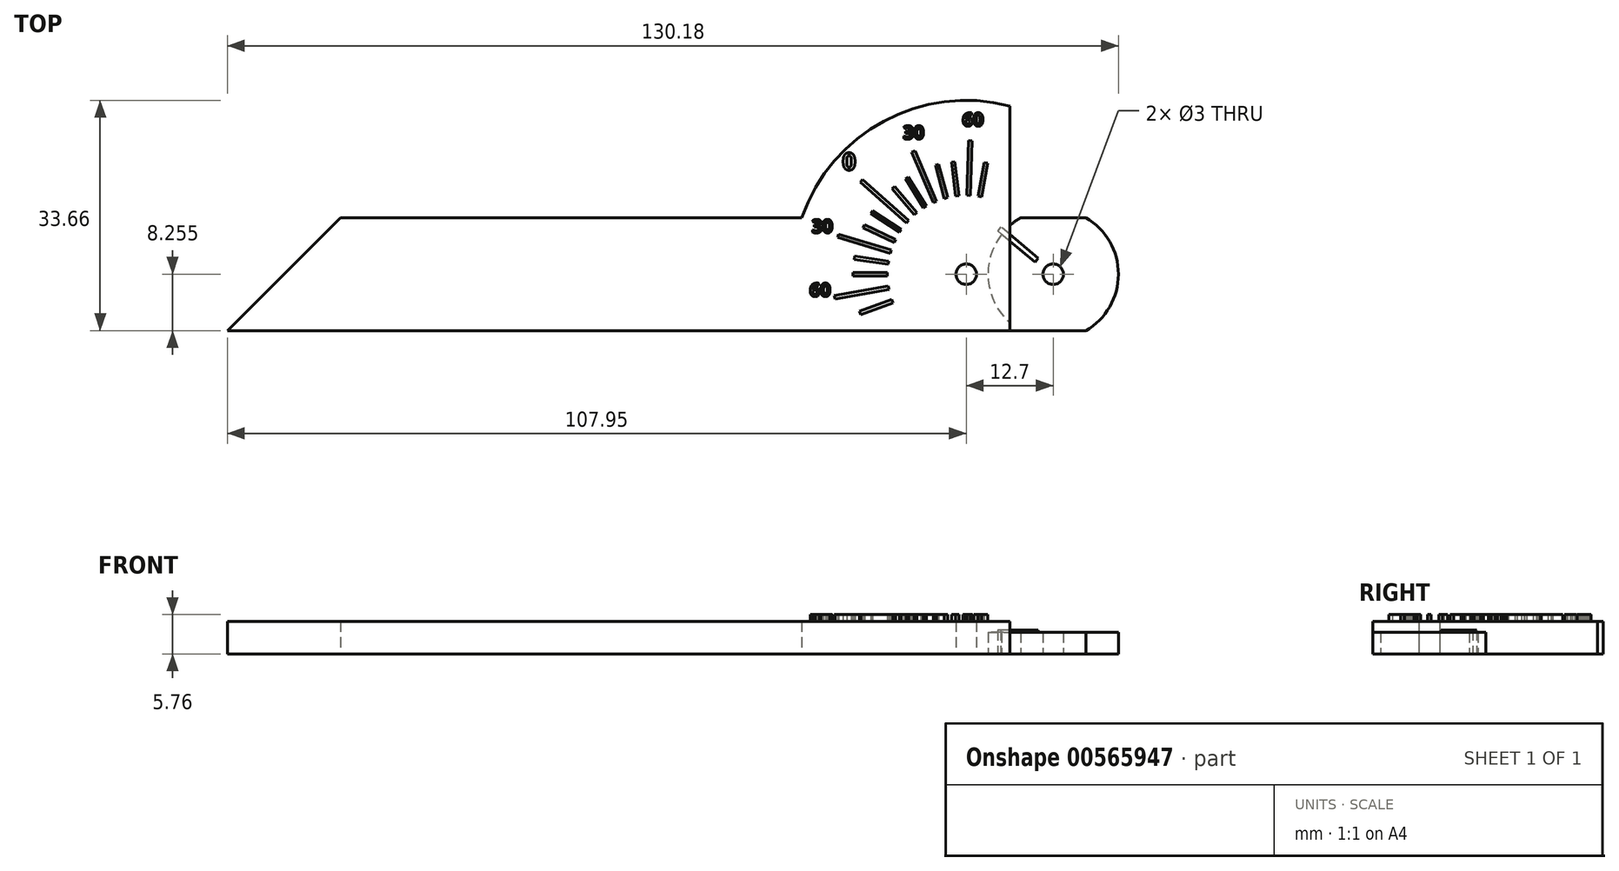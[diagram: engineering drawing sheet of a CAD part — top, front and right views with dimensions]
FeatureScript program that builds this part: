
annotation { "Feature Type Name" : "Feature", "Feature Type Description" : "" }
export const myFeature = defineFeature(function(context is Context, id is Id, definition is map)
    precondition{}
    {
        {
            var Q0;
            Q0=qCreatedBy(makeId("Top.planeOp"),FACE);
            var sketch = newSketch(context, id + "F0", { "sketchPlane" : qUnion([Q0])});
            skLineSegment(sketch, "E0.bottom", {"start": v(0, 0) * mm, "end": v(114.3, 0) * mm});
            skLineSegment(sketch, "E0.top", {"start": v(0, 16.51) * mm, "end": v(97.79, 16.51) * mm});
            skLineSegment(sketch, "E0.left", {"start": v(0, 0) * mm, "end": v(0, 16.51) * mm});
            skLineSegment(sketch, "E1", {"start": v(114.3, 0) * mm, "end": v(97.79, 16.51) * mm});
            skCircle(sketch, "E2", {"center": v(6.35, 8.26) * mm, "radius": 9.53 * mm});
            skPoint(sketch, "E2.centerSnap0", {"position": v(0, 8.26) * mm});
            skLineSegment(sketch, "E3", {"start": v(-7.35, 8.26) * mm, "end": v(-3.17, 8.26) * mm, "construction": true});
            skCircle(sketch, "E4", {"center": v(6.35, 8.26) * mm, "radius": 1.5 * mm});
            skLineSegment(sketch, "E5", {"start": v(11.1, 0) * mm, "end": v(0, 0) * mm});
            skLineSegment(sketch, "E6", {"start": v(11.1, 16.51) * mm, "end": v(0, 16.51) * mm});
            skLineSegment(sketch, "E7", {"start": v(6.35, 8.26) * mm, "end": v(-14.53, 8.26) * mm, "construction": true});
            skLineSegment(sketch, "E8", {"start": v(-14.53, 8.26) * mm, "end": v(6.35, 8.26) * mm, "construction": true});
            skLineSegment(sketch, "E9", {"start": v(6.35, 8.25) * mm, "end": v(-8.62, 20.82) * mm, "construction": true});
            skLineSegment(sketch, "E10", {"start": v(3.92, 10.3) * mm, "end": v(4.16, 10.58) * mm});
            skLineSegment(sketch, "E11", {"start": v(4.16, 10.58) * mm, "end": v(-1.3, 15.16) * mm});
            skLineSegment(sketch, "E12", {"start": v(-1.3, 15.16) * mm, "end": v(-1.54, 14.87) * mm});
            skLineSegment(sketch, "E13.MirrorCS", {"start": v(-1.78, 14.59) * mm, "end": v(-1.54, 14.87) * mm});
            skLineSegment(sketch, "E14.MirrorCS", {"start": v(3.68, 10) * mm, "end": v(-1.78, 14.59) * mm});
            skLineSegment(sketch, "E15.MirrorCS", {"start": v(3.92, 10.3) * mm, "end": v(3.68, 10) * mm});
            skPoint(sketch, "E16", {"position": v(-0.7, 14.66) * mm});
            skPoint(sketch, "E17.orphan", {"position": v(0, 9.02) * mm});
            skPoint(sketch, "E18.MirrorCS.start.orphan", {"position": v(-7.35, 9.02) * mm});
            skPoint(sketch, "E19.orphan", {"position": v(0, 7.49) * mm});
            skPoint(sketch, "E20.end.orphan", {"position": v(-7.35, 7.49) * mm});
            skPoint(sketch, "E21.MirrorCS.start.orphan", {"position": v(-7.35, 8.26) * mm});
            skSolve(sketch);
        }
        {
            var Q0;
            {var subQ0=sQuery(id+"F0.wireOp",EDGE,"E0.bottom");Q0=makeQuery(id+"F0.imprint","IMPRINT",FACE,{"disambiguationData":[TD([[makeQuery(id+"F0.imprint","IMPRINT",EDGE,{"derivedFrom":subQ0}),1.0]])]});}
            var Q1;
            Q1=makeQuery(id+"F0.imprint","IMPRINT",FACE,{"disambiguationData":[TD([[makeQuery(id+"F0.imprint","IMPRINT",EDGE,{"derivedFrom":sQuery(id+"F0.wireOp",EDGE,"E4")}),-1.0]])]});
            var Q2;
            {var subQ0=sQuery(id+"F0.wireOp",EDGE,"E2");var subQ1=sQuery(id+"F0.wireOp",EDGE,"E0.left");var subQ2=makeQuery(id+"F0.imprint","INTERSECT",VERTEX,{"disambiguationData":[OD(0.0)],"derivedFrom":[subQ1,subQ0]});Q2=makeQuery(id+"F0.imprint","IMPRINT",FACE,{"disambiguationData":[TD([[makeQuery(id+"F0.imprint","IMPRINT",EDGE,{"disambiguationData":[TD([[subQ2,-1.0]])],"derivedFrom":subQ1}),1.0]])]});}
            extrude(context, id + "F1", {"entities" : qUnion([Q0, Q1, Q2]), "depth" : 3.17 * mm, "offsetDistance" : 25.4 * mm});
        }
        {
            var Q0;
            {var subQ5=sQuery(id+"F0.wireOp",EDGE,"E0.left");var subQ7=sQuery(id+"F0.wireOp",EDGE,"E14.MirrorCS");var subQ9=makeQuery(id+"F0.imprint","INTERSECT",VERTEX,{"derivedFrom":[subQ5,subQ7]});Q0=makeQuery(id+"F0.imprint","IMPRINT",FACE,{"disambiguationData":[TD([[makeQuery(id+"F0.imprint","IMPRINT",EDGE,{"disambiguationData":[TD([[subQ9,-1.0]])],"derivedFrom":subQ5}),1.0]])]});}
            var Q1;
            {var subQ1=sQuery(id+"F0.wireOp",EDGE,"E10");Q1=makeQuery(id+"F0.imprint","IMPRINT",FACE,{"disambiguationData":[TD([[makeQuery(id+"F0.imprint","IMPRINT",EDGE,{"derivedFrom":subQ1}),1.0]])]});}
            var Q2;
            {var subQ0=sQuery(id+"F0.wireOp",EDGE,"E12");Q2=makeQuery(id+"F0.imprint","IMPRINT",FACE,{"disambiguationData":[TD([[makeQuery(id+"F0.imprint","IMPRINT",EDGE,{"derivedFrom":subQ0}),1.0]])]});}
            var Q3;
            {var subQ0=sQuery(id+"F0.wireOp",EDGE,"E13.MirrorCS");Q3=makeQuery(id+"F0.imprint","IMPRINT",FACE,{"disambiguationData":[TD([[makeQuery(id+"F0.imprint","IMPRINT",EDGE,{"derivedFrom":subQ0}),-1.0]])]});}
            extrude(context, id + "F2", {"entities" : qUnion([Q0, Q1, Q2, Q3]), "operationType" : NewBodyOperationType.ADD, "depth" : 3.5 * mm, "offsetDistance" : 25.4 * mm});
        }
        {
            var Q0;
            Q0=qCreatedBy(makeId("Top.planeOp"),FACE);
            var sketch = newSketch(context, id + "F3", { "sketchPlane" : qUnion([Q0])});
            skLineSegment(sketch, "E22.bottom", {"start": v(0, 0) * mm, "end": v(-114.3, 0) * mm});
            skLineSegment(sketch, "E22.top", {"start": v(0, 16.51) * mm, "end": v(-97.8, 16.51) * mm});
            skLineSegment(sketch, "E22.left", {"start": v(0, 0) * mm, "end": v(0, 16.51) * mm});
            skLineSegment(sketch, "E23", {"start": v(-114.3, 0) * mm, "end": v(-97.8, 16.5) * mm});
            skCircle(sketch, "E24", {"center": v(-6.35, 8.26) * mm, "radius": 25.4 * mm});
            skPoint(sketch, "E24.centerSnap0", {"position": v(0, 8.26) * mm});
            skLineSegment(sketch, "E25", {"start": v(-6.35, 8.26) * mm, "end": v(0, 8.26) * mm});
            skLineSegment(sketch, "E26", {"start": v(0, 16.51) * mm, "end": v(17.67, 16.51) * mm});
            skLineSegment(sketch, "E27", {"start": v(0, 0) * mm, "end": v(17.67, 0) * mm});
            skCircle(sketch, "E28", {"center": v(-6.35, 8.26) * mm, "radius": 1.5 * mm});
            skLineSegment(sketch, "E29", {"start": v(0, 16.51) * mm, "end": v(0, 32.85) * mm});
            skSolve(sketch);
        }
        {
            var Q0;
            {var subQ0=sQuery(id+"F3.wireOp",EDGE,"E23");Q0=makeQuery(id+"F3.imprint","IMPRINT",FACE,{"disambiguationData":[TD([[makeQuery(id+"F3.imprint","IMPRINT",EDGE,{"derivedFrom":subQ0}),-1.0]])]});}
            var Q1;
            Q1=makeQuery(id+"F3.imprint","IMPRINT",FACE,{"disambiguationData":[TD([[makeQuery(id+"F3.imprint","IMPRINT",EDGE,{"derivedFrom":sQuery(id+"F3.wireOp",EDGE,"E28")}),-1.0]])]});
            var Q2;
            {var subQ0=sQuery(id+"F3.wireOp",EDGE,"E29");Q2=makeQuery(id+"F3.imprint","IMPRINT",FACE,{"disambiguationData":[TD([[makeQuery(id+"F3.imprint","IMPRINT",EDGE,{"derivedFrom":subQ0}),1.0]])]});}
            extrude(context, id + "F4", {"entities" : qUnion([Q0, Q1, Q2]), "depth" : 4.76 * mm, "offsetDistance" : 25.4 * mm});
        }
        {
            var Q0;
            Q0=makeQuery(id+"F4.opExtrude","CAP_FACE",FACE,{"disambiguationData":[OSD([sQuery(id+"F3.wireOp",EDGE,"E22.bottom"),sQuery(id+"F3.wireOp",EDGE,"E22.top"),sQuery(id+"F3.wireOp",EDGE,"E22.left"),sQuery(id+"F3.wireOp",EDGE,"E23"),sQuery(id+"F3.wireOp",EDGE,"E24"),sQuery(id+"F3.wireOp",EDGE,"E28"),sQuery(id+"F3.wireOp",EDGE,"E29")])],"isStart":false});
            var sketch = newSketch(context, id + "F5", { "sketchPlane" : qUnion([Q0])});
            skCircle(sketch, "E30", {"center": v(-6.35, 8.26) * mm, "radius": 9.53 * mm});
            skCircle(sketch, "E31.0", {"center": v(-6.35, 8.26) * mm, "radius": 11.53 * mm});
            skLineSegment(sketch, "E32", {"start": v(-6.35, 8.26) * mm, "end": v(-38.76, 8.25) * mm, "construction": true});
            skLineSegment(sketch, "E33", {"start": v(-17.88, 8.25) * mm, "end": v(-17.88, 8.5) * mm});
            skLineSegment(sketch, "E34", {"start": v(-17.88, 8.5) * mm, "end": v(-22.88, 8.5) * mm});
            skLineSegment(sketch, "E35", {"start": v(-22.88, 8.5) * mm, "end": v(-22.88, 8.25) * mm});
            skLineSegment(sketch, "E36.MirrorCS", {"start": v(-17.88, 8) * mm, "end": v(-22.88, 8) * mm});
            skLineSegment(sketch, "E37.MirrorCS", {"start": v(-22.88, 8) * mm, "end": v(-22.88, 8.25) * mm});
            skLineSegment(sketch, "E38.MirrorCS", {"start": v(-17.88, 8.26) * mm, "end": v(-17.88, 8) * mm});
            skSolve(sketch);
        }
        {
            var Q0;
            {var subQ2=sQuery(id+"F5.wireOp",EDGE,"E33");Q0=makeQuery(id+"F5.imprint","IMPRINT",FACE,{"disambiguationData":[TD([[makeQuery(id+"F5.imprint","IMPRINT",EDGE,{"derivedFrom":subQ2}),-1.0]])]});}
            var sketch = newSketch(context, id + "F6", { "sketchPlane" : qUnion([Q0])});
            skLineSegment(sketch, "E39.0", {"start": v(-17.88, 8.25) * mm, "end": v(-17.88, 8.5) * mm});
            skLineSegment(sketch, "E40.0", {"start": v(-17.88, 8.26) * mm, "end": v(-17.88, 8) * mm});
            skLineSegment(sketch, "E41.0", {"start": v(-17.88, 8) * mm, "end": v(-22.88, 8) * mm});
            skLineSegment(sketch, "E42.0", {"start": v(-17.88, 8.5) * mm, "end": v(-22.88, 8.5) * mm});
            skLineSegment(sketch, "E43.0", {"start": v(-22.88, 8.5) * mm, "end": v(-22.88, 8.25) * mm});
            skLineSegment(sketch, "E44.0", {"start": v(-22.88, 8) * mm, "end": v(-22.88, 8.25) * mm});
            skPoint(sketch, "E45.0", {"position": v(-6.35, 8.26) * mm});
            skLineSegment(sketch, "E46", {"start": v(-22.88, 8) * mm, "end": v(-17.88, 8.5) * mm, "construction": true});
            skLineSegment(sketch, "E47", {"start": v(-22.88, 8.5) * mm, "end": v(-17.88, 8) * mm, "construction": true});
            skPoint(sketch, "E48", {"position": v(-20.38, 8.25) * mm});
            skLineSegment(sketch, "E49.1.0", {"start": v(-17.79, 9.68) * mm, "end": v(-22.74, 10.4) * mm});
            skLineSegment(sketch, "E49.1.1", {"start": v(-22.74, 10.4) * mm, "end": v(-17.72, 10.17) * mm, "construction": true});
            skLineSegment(sketch, "E49.1.2", {"start": v(-22.66, 10.9) * mm, "end": v(-17.79, 9.68) * mm, "construction": true});
            skLineSegment(sketch, "E49.1.3", {"start": v(-17.75, 9.93) * mm, "end": v(-17.72, 10.17) * mm});
            skLineSegment(sketch, "E49.1.4", {"start": v(-17.75, 9.93) * mm, "end": v(-17.79, 9.68) * mm});
            skLineSegment(sketch, "E49.1.5", {"start": v(-22.66, 10.9) * mm, "end": v(-17.72, 10.17) * mm});
            skLineSegment(sketch, "E49.1.6", {"start": v(-22.74, 10.4) * mm, "end": v(-22.7, 10.65) * mm});
            skLineSegment(sketch, "E49.1.7", {"start": v(-22.66, 10.9) * mm, "end": v(-22.7, 10.65) * mm});
            skPoint(sketch, "E49.1.8", {"position": v(-20.23, 10.29) * mm});
            skLineSegment(sketch, "E49.2.0", {"start": v(-17.46, 11.32) * mm, "end": v(-22.25, 12.75) * mm});
            skLineSegment(sketch, "E49.2.1", {"start": v(-22.25, 12.75) * mm, "end": v(-17.32, 11.8) * mm, "construction": true});
            skLineSegment(sketch, "E49.2.2", {"start": v(-22.1, 13.23) * mm, "end": v(-17.46, 11.32) * mm, "construction": true});
            skLineSegment(sketch, "E49.2.3", {"start": v(-17.4, 11.56) * mm, "end": v(-17.32, 11.8) * mm});
            skLineSegment(sketch, "E49.2.4", {"start": v(-17.4, 11.56) * mm, "end": v(-17.46, 11.32) * mm});
            skLineSegment(sketch, "E49.2.5", {"start": v(-22.1, 13.23) * mm, "end": v(-17.32, 11.8) * mm});
            skLineSegment(sketch, "E49.2.6", {"start": v(-22.25, 12.75) * mm, "end": v(-22.18, 13) * mm});
            skLineSegment(sketch, "E49.2.7", {"start": v(-22.1, 13.23) * mm, "end": v(-22.18, 13) * mm});
            skPoint(sketch, "E49.2.8", {"position": v(-19.79, 12.28) * mm});
            skLineSegment(sketch, "E49.3.0", {"start": v(-16.9, 12.9) * mm, "end": v(-21.43, 15.01) * mm});
            skLineSegment(sketch, "E49.3.1", {"start": v(-21.43, 15.01) * mm, "end": v(-16.69, 13.35) * mm, "construction": true});
            skLineSegment(sketch, "E49.3.2", {"start": v(-21.22, 15.47) * mm, "end": v(-16.9, 12.9) * mm, "construction": true});
            skLineSegment(sketch, "E49.3.3", {"start": v(-16.8, 13.13) * mm, "end": v(-16.69, 13.35) * mm});
            skLineSegment(sketch, "E49.3.4", {"start": v(-16.8, 13.13) * mm, "end": v(-16.9, 12.9) * mm});
            skLineSegment(sketch, "E49.3.5", {"start": v(-21.22, 15.47) * mm, "end": v(-16.69, 13.35) * mm});
            skLineSegment(sketch, "E49.3.6", {"start": v(-21.43, 15.01) * mm, "end": v(-21.33, 15.24) * mm});
            skLineSegment(sketch, "E49.3.7", {"start": v(-21.22, 15.47) * mm, "end": v(-21.33, 15.24) * mm});
            skPoint(sketch, "E49.3.8", {"position": v(-19.06, 14.18) * mm});
            skLineSegment(sketch, "E49.4.0", {"start": v(-16.12, 14.38) * mm, "end": v(-20.3, 17.13) * mm});
            skLineSegment(sketch, "E49.4.1", {"start": v(-20.3, 17.13) * mm, "end": v(-15.84, 14.8) * mm, "construction": true});
            skLineSegment(sketch, "E49.4.2", {"start": v(-20.02, 17.54) * mm, "end": v(-16.12, 14.38) * mm, "construction": true});
            skLineSegment(sketch, "E49.4.3", {"start": v(-15.98, 14.59) * mm, "end": v(-15.84, 14.8) * mm});
            skLineSegment(sketch, "E49.4.4", {"start": v(-15.98, 14.59) * mm, "end": v(-16.12, 14.38) * mm});
            skLineSegment(sketch, "E49.4.5", {"start": v(-20.02, 17.54) * mm, "end": v(-15.84, 14.8) * mm});
            skLineSegment(sketch, "E49.4.6", {"start": v(-20.3, 17.13) * mm, "end": v(-20.16, 17.34) * mm});
            skLineSegment(sketch, "E49.4.7", {"start": v(-20.02, 17.54) * mm, "end": v(-20.16, 17.34) * mm});
            skPoint(sketch, "E49.4.8", {"position": v(-18.07, 15.96) * mm});
            skLineSegment(sketch, "E49.5.0", {"start": v(-15.13, 15.73) * mm, "end": v(-18.86, 19.05) * mm});
            skLineSegment(sketch, "E49.5.1", {"start": v(-18.86, 19.05) * mm, "end": v(-14.8, 16.1) * mm, "construction": true});
            skLineSegment(sketch, "E49.5.2", {"start": v(-18.53, 19.43) * mm, "end": v(-15.13, 15.73) * mm, "construction": true});
            skLineSegment(sketch, "E49.5.3", {"start": v(-14.96, 15.92) * mm, "end": v(-14.8, 16.1) * mm});
            skLineSegment(sketch, "E49.5.4", {"start": v(-14.96, 15.92) * mm, "end": v(-15.13, 15.73) * mm});
            skLineSegment(sketch, "E49.5.5", {"start": v(-18.53, 19.43) * mm, "end": v(-14.8, 16.1) * mm});
            skLineSegment(sketch, "E49.5.6", {"start": v(-18.86, 19.05) * mm, "end": v(-18.7, 19.24) * mm});
            skLineSegment(sketch, "E49.5.7", {"start": v(-18.53, 19.43) * mm, "end": v(-18.7, 19.24) * mm});
            skPoint(sketch, "E49.5.8", {"position": v(-16.83, 17.58) * mm});
            skLineSegment(sketch, "E49.6.0", {"start": v(-13.95, 16.92) * mm, "end": v(-17.16, 20.75) * mm});
            skLineSegment(sketch, "E49.6.1", {"start": v(-17.16, 20.75) * mm, "end": v(-13.57, 17.24) * mm, "construction": true});
            skLineSegment(sketch, "E49.6.2", {"start": v(-16.78, 21.07) * mm, "end": v(-13.95, 16.92) * mm, "construction": true});
            skLineSegment(sketch, "E49.6.3", {"start": v(-13.76, 17.08) * mm, "end": v(-13.57, 17.24) * mm});
            skLineSegment(sketch, "E49.6.4", {"start": v(-13.76, 17.08) * mm, "end": v(-13.95, 16.92) * mm});
            skLineSegment(sketch, "E49.6.5", {"start": v(-16.78, 21.07) * mm, "end": v(-13.57, 17.24) * mm});
            skLineSegment(sketch, "E49.6.6", {"start": v(-17.16, 20.75) * mm, "end": v(-16.97, 20.91) * mm});
            skLineSegment(sketch, "E49.6.7", {"start": v(-16.78, 21.07) * mm, "end": v(-16.97, 20.91) * mm});
            skPoint(sketch, "E49.6.8", {"position": v(-15.37, 19) * mm});
            skLineSegment(sketch, "E49.anchor1", {"start": v(-6.35, 8.26) * mm, "end": v(-20.38, 8.25) * mm, "construction": true});
            skLineSegment(sketch, "E49.anchor2", {"start": v(-6.35, 8.26) * mm, "end": v(-3.91, 22.07) * mm, "construction": true});
            skPoint(sketch, "E50.0.7.0", {"position": v(-13.71, 20.2) * mm});
            skLineSegment(sketch, "E50.3.7.0", {"start": v(-15.24, 22.19) * mm, "end": v(-12.19, 18.2) * mm, "construction": true});
            skLineSegment(sketch, "E50.6.7.0", {"start": v(-14.81, 22.45) * mm, "end": v(-12.61, 17.93) * mm, "construction": true});
            skLineSegment(sketch, "E50.9.7.0", {"start": v(-12.4, 18.06) * mm, "end": v(-12.19, 18.2) * mm});
            skLineSegment(sketch, "E50.12.7.0", {"start": v(-12.4, 18.06) * mm, "end": v(-12.61, 17.93) * mm});
            skLineSegment(sketch, "E50.15.7.0", {"start": v(-14.81, 22.45) * mm, "end": v(-12.19, 18.2) * mm});
            skLineSegment(sketch, "E50.18.7.0", {"start": v(-15.24, 22.19) * mm, "end": v(-15.03, 22.32) * mm});
            skLineSegment(sketch, "E50.21.7.0", {"start": v(-14.81, 22.45) * mm, "end": v(-15.03, 22.32) * mm});
            skLineSegment(sketch, "E50.24.7.0", {"start": v(-12.61, 17.93) * mm, "end": v(-15.24, 22.19) * mm});
            skPoint(sketch, "E50.0.8.0", {"position": v(-11.9, 21.13) * mm});
            skLineSegment(sketch, "E50.3.8.0", {"start": v(-13.12, 23.33) * mm, "end": v(-10.69, 18.94) * mm, "construction": true});
            skLineSegment(sketch, "E50.6.8.0", {"start": v(-12.67, 23.53) * mm, "end": v(-11.14, 18.74) * mm, "construction": true});
            skLineSegment(sketch, "E50.9.8.0", {"start": v(-10.91, 18.84) * mm, "end": v(-10.69, 18.94) * mm});
            skLineSegment(sketch, "E50.12.8.0", {"start": v(-10.91, 18.84) * mm, "end": v(-11.14, 18.74) * mm});
            skLineSegment(sketch, "E50.15.8.0", {"start": v(-12.67, 23.53) * mm, "end": v(-10.69, 18.94) * mm});
            skLineSegment(sketch, "E50.18.8.0", {"start": v(-13.12, 23.33) * mm, "end": v(-12.9, 23.43) * mm});
            skLineSegment(sketch, "E50.21.8.0", {"start": v(-12.67, 23.53) * mm, "end": v(-12.9, 23.43) * mm});
            skLineSegment(sketch, "E50.24.8.0", {"start": v(-11.14, 18.74) * mm, "end": v(-13.12, 23.33) * mm});
            skPoint(sketch, "E50.0.9.0", {"position": v(-9.98, 21.8) * mm});
            skLineSegment(sketch, "E50.3.9.0", {"start": v(-10.87, 24.15) * mm, "end": v(-9.1, 19.45) * mm, "construction": true});
            skLineSegment(sketch, "E50.6.9.0", {"start": v(-10.39, 24.28) * mm, "end": v(-9.57, 19.32) * mm, "construction": true});
            skLineSegment(sketch, "E50.9.9.0", {"start": v(-9.33, 19.39) * mm, "end": v(-9.1, 19.45) * mm});
            skLineSegment(sketch, "E50.12.9.0", {"start": v(-9.33, 19.39) * mm, "end": v(-9.57, 19.32) * mm});
            skLineSegment(sketch, "E50.15.9.0", {"start": v(-10.39, 24.28) * mm, "end": v(-9.1, 19.45) * mm});
            skLineSegment(sketch, "E50.18.9.0", {"start": v(-10.87, 24.15) * mm, "end": v(-10.63, 24.22) * mm});
            skLineSegment(sketch, "E50.21.9.0", {"start": v(-10.39, 24.28) * mm, "end": v(-10.63, 24.22) * mm});
            skLineSegment(sketch, "E50.24.9.0", {"start": v(-9.57, 19.32) * mm, "end": v(-10.87, 24.15) * mm});
            skPoint(sketch, "E50.0.10.0", {"position": v(-7.98, 22.19) * mm});
            skLineSegment(sketch, "E50.3.10.0", {"start": v(-8.52, 24.64) * mm, "end": v(-7.44, 19.73) * mm, "construction": true});
            skLineSegment(sketch, "E50.6.10.0", {"start": v(-8.02, 24.7) * mm, "end": v(-7.94, 19.67) * mm, "construction": true});
            skLineSegment(sketch, "E50.9.10.0", {"start": v(-7.69, 19.7) * mm, "end": v(-7.44, 19.73) * mm});
            skLineSegment(sketch, "E50.12.10.0", {"start": v(-7.69, 19.7) * mm, "end": v(-7.94, 19.67) * mm});
            skLineSegment(sketch, "E50.15.10.0", {"start": v(-8.02, 24.7) * mm, "end": v(-7.44, 19.73) * mm});
            skLineSegment(sketch, "E50.18.10.0", {"start": v(-8.52, 24.64) * mm, "end": v(-8.27, 24.67) * mm});
            skLineSegment(sketch, "E50.21.10.0", {"start": v(-8.02, 24.7) * mm, "end": v(-8.27, 24.67) * mm});
            skLineSegment(sketch, "E50.24.10.0", {"start": v(-7.94, 19.67) * mm, "end": v(-8.52, 24.64) * mm});
            skPoint(sketch, "E50.0.11.0", {"position": v(-5.94, 22.27) * mm});
            skLineSegment(sketch, "E50.3.11.0", {"start": v(-6.12, 24.78) * mm, "end": v(-5.76, 19.77) * mm, "construction": true});
            skLineSegment(sketch, "E50.6.11.0", {"start": v(-5.62, 24.77) * mm, "end": v(-6.26, 19.78) * mm, "construction": true});
            skLineSegment(sketch, "E50.9.11.0", {"start": v(-6.01, 19.78) * mm, "end": v(-5.76, 19.77) * mm});
            skLineSegment(sketch, "E50.12.11.0", {"start": v(-6.01, 19.78) * mm, "end": v(-6.26, 19.78) * mm});
            skLineSegment(sketch, "E50.15.11.0", {"start": v(-5.62, 24.77) * mm, "end": v(-5.76, 19.77) * mm});
            skLineSegment(sketch, "E50.18.11.0", {"start": v(-6.12, 24.78) * mm, "end": v(-5.87, 24.77) * mm});
            skLineSegment(sketch, "E50.21.11.0", {"start": v(-5.62, 24.77) * mm, "end": v(-5.87, 24.77) * mm});
            skLineSegment(sketch, "E50.24.11.0", {"start": v(-6.26, 19.78) * mm, "end": v(-6.12, 24.78) * mm});
            skLineSegment(sketch, "E51.1.0", {"start": v(-17.66, 6) * mm, "end": v(-22.58, 5.14) * mm});
            skLineSegment(sketch, "E51.1.1", {"start": v(-22.58, 5.14) * mm, "end": v(-17.74, 6.5) * mm, "construction": true});
            skLineSegment(sketch, "E51.1.2", {"start": v(-22.67, 5.63) * mm, "end": v(-17.66, 6) * mm, "construction": true});
            skLineSegment(sketch, "E51.1.3", {"start": v(-17.7, 6.25) * mm, "end": v(-17.74, 6.5) * mm});
            skLineSegment(sketch, "E51.1.4", {"start": v(-17.7, 6.25) * mm, "end": v(-17.66, 6) * mm});
            skLineSegment(sketch, "E51.1.5", {"start": v(-22.67, 5.63) * mm, "end": v(-17.74, 6.5) * mm});
            skLineSegment(sketch, "E51.1.6", {"start": v(-22.58, 5.14) * mm, "end": v(-22.62, 5.39) * mm});
            skLineSegment(sketch, "E51.1.7", {"start": v(-22.67, 5.63) * mm, "end": v(-22.62, 5.39) * mm});
            skPoint(sketch, "E51.1.8", {"position": v(-20.16, 5.82) * mm});
            skLineSegment(sketch, "E51.2.0", {"start": v(-17.1, 4.08) * mm, "end": v(-21.8, 2.37) * mm});
            skLineSegment(sketch, "E51.2.1", {"start": v(-21.8, 2.37) * mm, "end": v(-17.27, 4.55) * mm, "construction": true});
            skLineSegment(sketch, "E51.2.2", {"start": v(-21.96, 2.84) * mm, "end": v(-17.1, 4.08) * mm, "construction": true});
            skLineSegment(sketch, "E51.2.3", {"start": v(-17.18, 4.31) * mm, "end": v(-17.27, 4.55) * mm});
            skLineSegment(sketch, "E51.2.4", {"start": v(-17.18, 4.31) * mm, "end": v(-17.1, 4.08) * mm});
            skLineSegment(sketch, "E51.2.5", {"start": v(-21.96, 2.84) * mm, "end": v(-17.27, 4.55) * mm});
            skLineSegment(sketch, "E51.2.6", {"start": v(-21.8, 2.37) * mm, "end": v(-21.88, 2.6) * mm});
            skLineSegment(sketch, "E51.2.7", {"start": v(-21.96, 2.84) * mm, "end": v(-21.88, 2.6) * mm});
            skPoint(sketch, "E51.2.8", {"position": v(-19.53, 3.46) * mm});
            skLineSegment(sketch, "E51.anchor2", {"start": v(-6.35, 8.26) * mm, "end": v(-19.53, 3.46) * mm, "construction": true});
            skPoint(sketch, "E52.0.12.0", {"position": v(-3.91, 22.07) * mm});
            skLineSegment(sketch, "E52.3.12.0", {"start": v(-3.73, 24.57) * mm, "end": v(-4.1, 19.56) * mm, "construction": true});
            skLineSegment(sketch, "E52.6.12.0", {"start": v(-3.23, 24.49) * mm, "end": v(-4.6, 19.65) * mm, "construction": true});
            skLineSegment(sketch, "E52.9.12.0", {"start": v(-4.35, 19.6) * mm, "end": v(-4.1, 19.56) * mm});
            skLineSegment(sketch, "E52.12.12.0", {"start": v(-4.35, 19.6) * mm, "end": v(-4.6, 19.65) * mm});
            skLineSegment(sketch, "E52.15.12.0", {"start": v(-3.23, 24.49) * mm, "end": v(-4.1, 19.56) * mm});
            skLineSegment(sketch, "E52.18.12.0", {"start": v(-3.73, 24.57) * mm, "end": v(-3.48, 24.53) * mm});
            skLineSegment(sketch, "E52.21.12.0", {"start": v(-3.23, 24.49) * mm, "end": v(-3.48, 24.53) * mm});
            skLineSegment(sketch, "E52.24.12.0", {"start": v(-4.6, 19.65) * mm, "end": v(-3.73, 24.57) * mm});
            skSolve(sketch);
        }
        {
            var Q0;
            Q0=makeQuery(id+"F6.imprint","IMPRINT",FACE,{"disambiguationData":[TD([[makeQuery(id+"F6.imprint","IMPRINT",EDGE,{"derivedFrom":sQuery(id+"F6.wireOp",EDGE,"E39.0")}),1.0]])]});
            var Q1;
            Q1=makeQuery(id+"F6.imprint","IMPRINT",FACE,{"disambiguationData":[TD([[makeQuery(id+"F6.imprint","IMPRINT",EDGE,{"derivedFrom":sQuery(id+"F6.wireOp",EDGE,"E49.1.0")}),-1.0]])]});
            var Q2;
            Q2=makeQuery(id+"F6.imprint","IMPRINT",FACE,{"disambiguationData":[TD([[makeQuery(id+"F6.imprint","IMPRINT",EDGE,{"derivedFrom":sQuery(id+"F6.wireOp",EDGE,"E49.2.0")}),-1.0]])]});
            var Q3;
            Q3=makeQuery(id+"F6.imprint","IMPRINT",FACE,{"disambiguationData":[TD([[makeQuery(id+"F6.imprint","IMPRINT",EDGE,{"derivedFrom":sQuery(id+"F6.wireOp",EDGE,"E49.3.0")}),-1.0]])]});
            var Q4;
            Q4=makeQuery(id+"F6.imprint","IMPRINT",FACE,{"disambiguationData":[TD([[makeQuery(id+"F6.imprint","IMPRINT",EDGE,{"derivedFrom":sQuery(id+"F6.wireOp",EDGE,"E49.4.0")}),-1.0]])]});
            var Q5;
            Q5=makeQuery(id+"F6.imprint","IMPRINT",FACE,{"disambiguationData":[TD([[makeQuery(id+"F6.imprint","IMPRINT",EDGE,{"derivedFrom":sQuery(id+"F6.wireOp",EDGE,"E49.5.0")}),-1.0]])]});
            var Q6;
            Q6=makeQuery(id+"F6.imprint","IMPRINT",FACE,{"disambiguationData":[TD([[makeQuery(id+"F6.imprint","IMPRINT",EDGE,{"derivedFrom":sQuery(id+"F6.wireOp",EDGE,"E49.6.0")}),-1.0]])]});
            var Q7;
            Q7=makeQuery(id+"F6.imprint","IMPRINT",FACE,{"disambiguationData":[TD([[makeQuery(id+"F6.imprint","IMPRINT",EDGE,{"derivedFrom":sQuery(id+"F6.wireOp",EDGE,"E50.9.7.0")}),1.0]])]});
            var Q8;
            Q8=makeQuery(id+"F6.imprint","IMPRINT",FACE,{"disambiguationData":[TD([[makeQuery(id+"F6.imprint","IMPRINT",EDGE,{"derivedFrom":sQuery(id+"F6.wireOp",EDGE,"E50.9.8.0")}),1.0]])]});
            var Q9;
            Q9=makeQuery(id+"F6.imprint","IMPRINT",FACE,{"disambiguationData":[TD([[makeQuery(id+"F6.imprint","IMPRINT",EDGE,{"derivedFrom":sQuery(id+"F6.wireOp",EDGE,"E50.9.9.0")}),1.0]])]});
            var Q10;
            Q10=makeQuery(id+"F6.imprint","IMPRINT",FACE,{"disambiguationData":[TD([[makeQuery(id+"F6.imprint","IMPRINT",EDGE,{"derivedFrom":sQuery(id+"F6.wireOp",EDGE,"E50.9.10.0")}),1.0]])]});
            var Q11;
            Q11=makeQuery(id+"F6.imprint","IMPRINT",FACE,{"disambiguationData":[TD([[makeQuery(id+"F6.imprint","IMPRINT",EDGE,{"derivedFrom":sQuery(id+"F6.wireOp",EDGE,"E50.9.11.0")}),1.0]])]});
            var Q12;
            Q12=makeQuery(id+"F6.imprint","IMPRINT",FACE,{"disambiguationData":[TD([[makeQuery(id+"F6.imprint","IMPRINT",EDGE,{"derivedFrom":sQuery(id+"F6.wireOp",EDGE,"E51.1.0")}),-1.0]])]});
            var Q13;
            Q13=makeQuery(id+"F6.imprint","IMPRINT",FACE,{"disambiguationData":[TD([[makeQuery(id+"F6.imprint","IMPRINT",EDGE,{"derivedFrom":sQuery(id+"F6.wireOp",EDGE,"E51.2.0")}),-1.0]])]});
            var Q14;
            Q14=makeQuery(id+"F6.imprint","IMPRINT",FACE,{"disambiguationData":[TD([[makeQuery(id+"F6.imprint","IMPRINT",EDGE,{"derivedFrom":sQuery(id+"F6.wireOp",EDGE,"E52.9.12.0")}),1.0]])]});
            extrude(context, id + "F7", {"entities" : qUnion([Q0, Q1, Q2, Q3, Q4, Q5, Q6, Q7, Q8, Q9, Q10, Q11, Q12, Q13, Q14]), "operationType" : NewBodyOperationType.ADD, "depth" : 1 * mm, "offsetDistance" : 25.4 * mm});
        }
        {
            var Q0;
            Q0=makeQuery(id+"F7.opExtrude","SWEPT_FACE",FACE,{"disambiguationData":[OSD([sQuery(id+"F6.wireOp",EDGE,"E50.18.11.0"),sQuery(id+"F6.wireOp",EDGE,"E50.21.11.0")])]});
            extrude(context, id + "F8", {"entities" : qUnion([Q0]), "operationType" : NewBodyOperationType.ADD, "depth" : 3 * mm, "offsetDistance" : 25.4 * mm});
        }
        {
            var Q0;
            Q0=makeQuery(id+"F7.opExtrude","SWEPT_FACE",FACE,{"disambiguationData":[OSD([sQuery(id+"F6.wireOp",EDGE,"E50.18.8.0"),sQuery(id+"F6.wireOp",EDGE,"E50.21.8.0")])]});
            extrude(context, id + "F9", {"entities" : qUnion([Q0]), "operationType" : NewBodyOperationType.ADD, "depth" : 3 * mm, "offsetDistance" : 25.4 * mm});
        }
        {
            var Q0;
            Q0=makeQuery(id+"F7.opExtrude","SWEPT_FACE",FACE,{"disambiguationData":[OSD([sQuery(id+"F6.wireOp",EDGE,"E49.5.6"),sQuery(id+"F6.wireOp",EDGE,"E49.5.7")])]});
            extrude(context, id + "F10", {"entities" : qUnion([Q0]), "operationType" : NewBodyOperationType.ADD, "depth" : 4 * mm, "offsetDistance" : 25.4 * mm});
        }
        {
            var Q0;
            Q0=makeQuery(id+"F7.opExtrude","SWEPT_FACE",FACE,{"disambiguationData":[OSD([sQuery(id+"F6.wireOp",EDGE,"E49.2.6"),sQuery(id+"F6.wireOp",EDGE,"E49.2.7")])]});
            extrude(context, id + "F11", {"entities" : qUnion([Q0]), "operationType" : NewBodyOperationType.ADD, "depth" : 3 * mm, "offsetDistance" : 25.4 * mm});
        }
        {
            var Q0;
            Q0=makeQuery(id+"F7.opExtrude","SWEPT_FACE",FACE,{"disambiguationData":[OSD([sQuery(id+"F6.wireOp",EDGE,"E51.1.6"),sQuery(id+"F6.wireOp",EDGE,"E51.1.7")])]});
            extrude(context, id + "F12", {"entities" : qUnion([Q0]), "operationType" : NewBodyOperationType.ADD, "depth" : 3 * mm, "offsetDistance" : 25.4 * mm});
        }
        {
            var Q0;
            {var subQ1=sQuery(id+"F6.wireOp",EDGE,"E39.0");Q0=makeQuery(id+"F6.imprint","IMPRINT",FACE,{"disambiguationData":[TD([[makeQuery(id+"F6.imprint","IMPRINT",EDGE,{"derivedFrom":subQ1}),-1.0]])]});}
            var sketch = newSketch(context, id + "F13", { "sketchPlane" : qUnion([Q0])});
            skText(sketch, "E53", { "text": "60", "fontName": "OpenSans-Bold.ttf"});
            skText(sketch, "E54", { "text": "30", "fontName": "OpenSans-Bold.ttf"});
            skText(sketch, "E55", { "text": "0", "fontName": "OpenSans-Bold.ttf"});
            skText(sketch, "E56", { "text": "30", "fontName": "OpenSans-Bold.ttf"});
            skText(sketch, "E57", { "text": "60", "fontName": "OpenSans-Bold.ttf"});
            const initialGuessF13  = {"E53": [-0.02925, 0.005, 1, 0, 0.00195], "E54": [-0.02894, 0.01431, 1, 0, 0.00195], "E55": [-0.02447, 0.02348, 1, 0, 0.00251], "E56": [-0.0156, 0.02801, 1, 0, 0.00195], "E57": [-0.00692, 0.0299, 1, 0, 0.00195]};
            skSetInitialGuess(sketch, initialGuessF13);
            skSolve(sketch);
        }
        {
            var Q0;
            Q0=makeQuery(id+"F13.imprint","IMPRINT",FACE,{"disambiguationData":[TD([[makeQuery(id+"F13.imprint","IMPRINT",EDGE,{"derivedFrom":sQuery(id+"F13.wireOp",EDGE,"E53.sketch_text.stroke-25")}),-1.0]])]});
            var Q1;
            Q1=makeQuery(id+"F13.imprint","IMPRINT",FACE,{"disambiguationData":[TD([[makeQuery(id+"F13.imprint","IMPRINT",EDGE,{"derivedFrom":sQuery(id+"F13.wireOp",EDGE,"E53.sketch_text.stroke-0")}),-1.0]])]});
            var Q2;
            Q2=makeQuery(id+"F13.imprint","IMPRINT",FACE,{"disambiguationData":[TD([[makeQuery(id+"F13.imprint","IMPRINT",EDGE,{"derivedFrom":sQuery(id+"F13.wireOp",EDGE,"E54.sketch_text.stroke-0")}),-1.0]])]});
            var Q3;
            Q3=makeQuery(id+"F13.imprint","IMPRINT",FACE,{"disambiguationData":[TD([[makeQuery(id+"F13.imprint","IMPRINT",EDGE,{"derivedFrom":sQuery(id+"F13.wireOp",EDGE,"E54.sketch_text.stroke-27")}),-1.0]])]});
            var Q4;
            Q4=makeQuery(id+"F13.imprint","IMPRINT",FACE,{"disambiguationData":[TD([[makeQuery(id+"F13.imprint","IMPRINT",EDGE,{"derivedFrom":sQuery(id+"F13.wireOp",EDGE,"E55.sketch_text.stroke-0")}),-1.0]])]});
            var Q5;
            Q5=makeQuery(id+"F13.imprint","IMPRINT",FACE,{"disambiguationData":[TD([[makeQuery(id+"F13.imprint","IMPRINT",EDGE,{"derivedFrom":sQuery(id+"F13.wireOp",EDGE,"E56.sketch_text.stroke-27")}),-1.0]])]});
            var Q6;
            Q6=makeQuery(id+"F13.imprint","IMPRINT",FACE,{"disambiguationData":[TD([[makeQuery(id+"F13.imprint","IMPRINT",EDGE,{"derivedFrom":sQuery(id+"F13.wireOp",EDGE,"E56.sketch_text.stroke-0")}),-1.0]])]});
            var Q7;
            Q7=makeQuery(id+"F13.imprint","IMPRINT",FACE,{"disambiguationData":[TD([[makeQuery(id+"F13.imprint","IMPRINT",EDGE,{"derivedFrom":sQuery(id+"F13.wireOp",EDGE,"E57.sketch_text.stroke-25")}),-1.0]])]});
            var Q8;
            Q8=makeQuery(id+"F13.imprint","IMPRINT",FACE,{"disambiguationData":[TD([[makeQuery(id+"F13.imprint","IMPRINT",EDGE,{"derivedFrom":sQuery(id+"F13.wireOp",EDGE,"E57.sketch_text.stroke-0")}),-1.0]])]});
            extrude(context, id + "F14", {"entities" : qUnion([Q0, Q1, Q2, Q3, Q4, Q5, Q6, Q7, Q8]), "operationType" : NewBodyOperationType.ADD, "depth" : 1 * mm, "offsetDistance" : 25.4 * mm});
        }
    });
